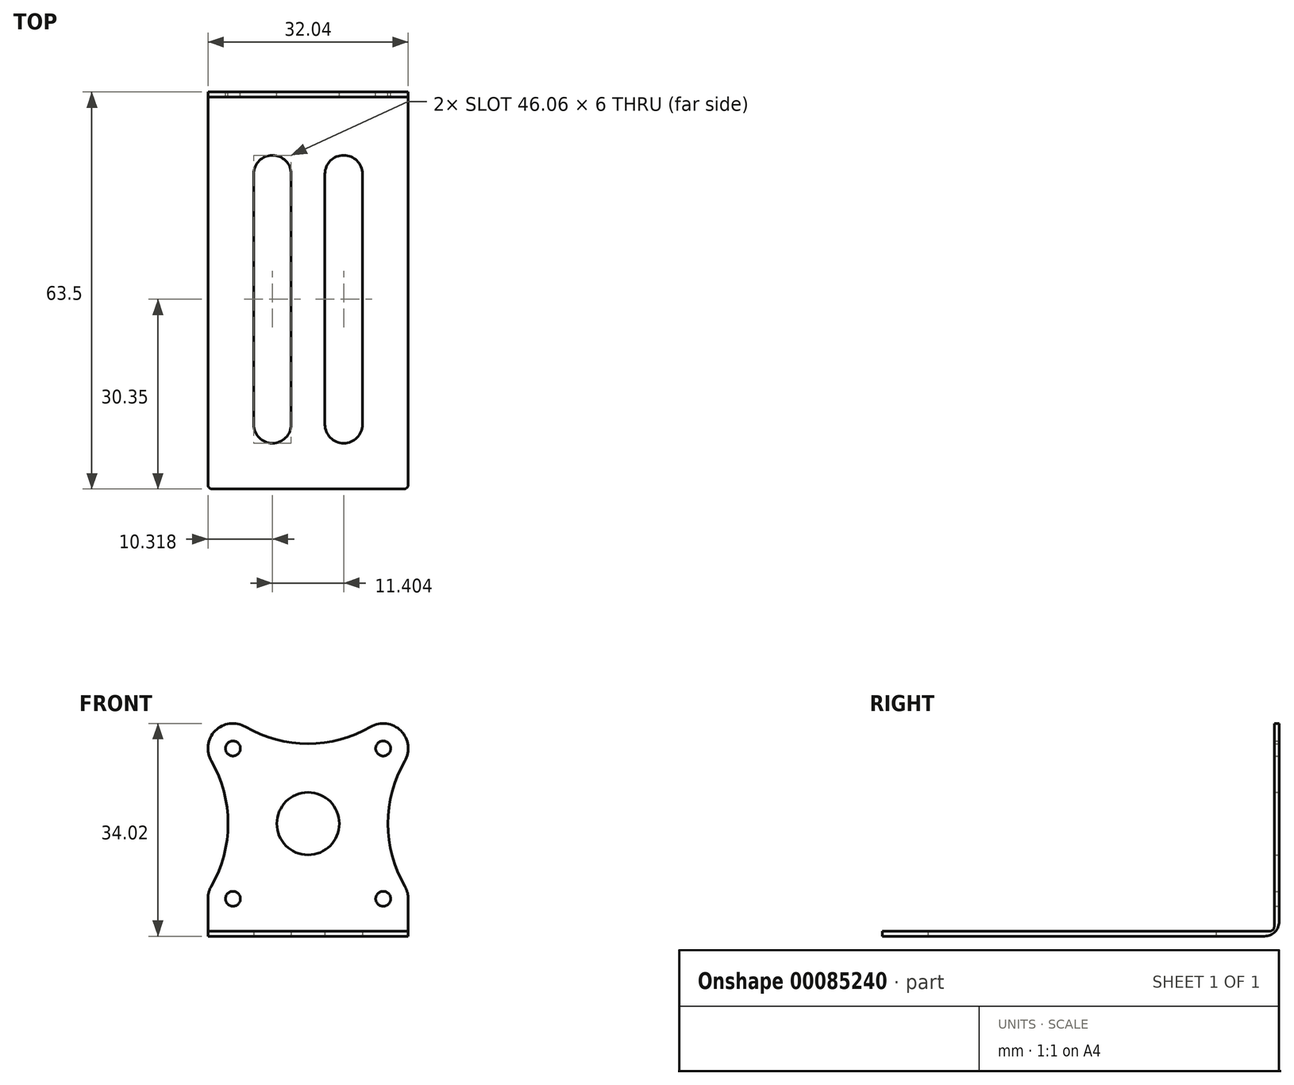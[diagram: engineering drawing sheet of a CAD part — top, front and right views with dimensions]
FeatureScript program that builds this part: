
annotation { "Feature Type Name" : "Feature", "Feature Type Description" : "" }
export const myFeature = defineFeature(function(context is Context, id is Id, definition is map)
    precondition{}
    {
        {
            assignVariable(context, id + "F0", {"name" : "thick", "anyValue" : .79});
        }
        {
            assignVariable(context, id + "F1", {"name" : "a", "anyValue" : .3125 + .375});
        }
        {
            var Q0;
            Q0=qCreatedBy(makeId("Front.planeOp"),FACE);
            var sketch = newSketch(context, id + "F2", { "sketchPlane" : qUnion([Q0])});
            skLineSegment(sketch, "E0.bottom", {"start": v(-12.02, 30.02) * mm, "end": v(12.02, 30.02) * mm, "construction": true});
            skLineSegment(sketch, "E0.top", {"start": v(-12.02, 5.98) * mm, "end": v(12.02, 5.98) * mm, "construction": true});
            skLineSegment(sketch, "E0.left", {"start": v(-12.02, 30.02) * mm, "end": v(-12.02, 5.98) * mm, "construction": true});
            skLineSegment(sketch, "E0.right", {"start": v(12.02, 30.02) * mm, "end": v(12.02, 5.98) * mm, "construction": true});
            skLineSegment(sketch, "E1", {"start": v(-12.02, 5.98) * mm, "end": v(12.02, 30.02) * mm, "construction": true});
            skPoint(sketch, "E2", {"position": v(0, 18) * mm});
            skCircle(sketch, "E3", {"center": v(-12.02, 30.02) * mm, "radius": 1.2 * mm});
            skCircle(sketch, "E4", {"center": v(12.02, 30.02) * mm, "radius": 1.2 * mm});
            skCircle(sketch, "E5", {"center": v(12.02, 5.98) * mm, "radius": 1.2 * mm});
            skCircle(sketch, "E6", {"center": v(-12.02, 5.98) * mm, "radius": 1.2 * mm});
            skCircle(sketch, "E7", {"center": v(0, 18) * mm, "radius": 14 * mm, "construction": true});
            skArc(sketch, "E8", {"start": v(-10.02, 33.48) * mm, "mid": v(0, 30.8) * mm, "end": v(10.02, 33.48) * mm});
            skArc(sketch, "E9", {"start": v(-15.48, 7.98) * mm, "mid": v(-12.8, 18) * mm, "end": v(-15.48, 28.02) * mm});
            skLineSegment(sketch, "E10", {"start": v(15.48, 28.02) * mm, "end": v(15.48, 28.02) * mm});
            skArc(sketch, "E11", {"start": v(-10.02, 33.48) * mm, "mid": v(-14.85, 32.85) * mm, "end": v(-15.48, 28.02) * mm});
            skArc(sketch, "E12", {"start": v(-15.48, 28.02) * mm, "mid": v(-9.2, 27.2) * mm, "end": v(-10.02, 33.48) * mm, "construction": true});
            skLineSegment(sketch, "E13", {"start": v(10.02, 33.48) * mm, "end": v(10.02, 33.48) * mm});
            skArc(sketch, "E14", {"start": v(15.48, 28.02) * mm, "mid": v(12.8, 18) * mm, "end": v(15.48, 7.98) * mm});
            skArc(sketch, "E15", {"start": v(-15.48, 7.98) * mm, "mid": v(-15.88, 7.02) * mm, "end": v(-16.02, 5.98) * mm});
            skArc(sketch, "E16", {"start": v(-16.02, 5.98) * mm, "mid": v(-8.16, 4.94) * mm, "end": v(-15.48, 7.98) * mm, "construction": true});
            skArc(sketch, "E17", {"start": v(15.48, 7.98) * mm, "mid": v(8.16, 4.94) * mm, "end": v(16.02, 5.98) * mm, "construction": true});
            skArc(sketch, "E18", {"start": v(16.02, 5.98) * mm, "mid": v(15.88, 7.02) * mm, "end": v(15.48, 7.98) * mm});
            skArc(sketch, "E19", {"start": v(10.02, 33.48) * mm, "mid": v(9.2, 27.2) * mm, "end": v(15.48, 28.02) * mm, "construction": true});
            skArc(sketch, "E20", {"start": v(15.48, 28.02) * mm, "mid": v(14.85, 32.85) * mm, "end": v(10.02, 33.48) * mm});
            skLineSegment(sketch, "E21", {"start": v(-16.02, 5.98) * mm, "end": v(-16.02, 0) * mm});
            skLineSegment(sketch, "E22", {"start": v(-16.02, 0) * mm, "end": v(16.02, 0) * mm});
            skLineSegment(sketch, "E23", {"start": v(16.02, 0) * mm, "end": v(16.02, 5.98) * mm});
            skCircle(sketch, "E24", {"center": v(0, 18) * mm, "radius": 5 * mm});
            skCircle(sketch, "E25", {"center": v(0, 18) * mm, "radius": 9.5 * mm, "construction": true});
            skCircle(sketch, "E26", {"center": v(0, 18) * mm, "radius": 8 * mm, "construction": true});
            skLineSegment(sketch, "E27", {"start": v(12.02, 5.98) * mm, "end": v(-12.02, 30.02) * mm, "construction": true});
            skSolve(sketch);
        }
        {
            var Q0;
            Q0 = qSketchRegion(id + "F2", true);
            extrude(context, id + "F3", {"entities" : qUnion([Q0]), "depth" : (getVariable(context, 'thick')) * mm});
        }
        {
            var Q0;
            Q0=qCreatedBy(makeId("Top.planeOp"),FACE);
            var sketch = newSketch(context, id + "F4", { "sketchPlane" : qUnion([Q0])});
            skLineSegment(sketch, "E28.bottom", {"start": v(-16.02, 0) * mm, "end": v(16.02, 0) * mm});
            skLineSegment(sketch, "E28.top", {"start": v(-16.02, -63.5) * mm, "end": v(16.02, -63.5) * mm});
            skLineSegment(sketch, "E28.left", {"start": v(-16.02, 0) * mm, "end": v(-16.02, -63.5) * mm});
            skLineSegment(sketch, "E28.right", {"start": v(16.02, 0) * mm, "end": v(16.02, -63.5) * mm});
            skSolve(sketch);
        }
        {
            var Q0;
            Q0 = qSketchRegion(id + "F4", true);
            extrude(context, id + "F5", {"entities" : qUnion([Q0]), "operationType" : NewBodyOperationType.ADD, "depth" : (getVariable(context, 'thick')) * mm});
        }
        {
            var Q0;
            Q0=makeQuery(id+"F5.boolean.opBoolean","INTERSECT",EDGE,{"derivedFrom":[makeQuery(id+"F3.opExtrude","CAP_FACE",FACE,{"disambiguationData":[OSD([sQuery(id+"F2.wireOp",EDGE,"E3"),sQuery(id+"F2.wireOp",EDGE,"E4"),sQuery(id+"F2.wireOp",EDGE,"E5"),sQuery(id+"F2.wireOp",EDGE,"E6"),sQuery(id+"F2.wireOp",EDGE,"E8"),sQuery(id+"F2.wireOp",EDGE,"E9"),sQuery(id+"F2.wireOp",EDGE,"E11"),sQuery(id+"F2.wireOp",EDGE,"E14"),sQuery(id+"F2.wireOp",EDGE,"E15"),sQuery(id+"F2.wireOp",EDGE,"E18"),sQuery(id+"F2.wireOp",EDGE,"E20"),sQuery(id+"F2.wireOp",EDGE,"E21"),sQuery(id+"F2.wireOp",EDGE,"E22"),sQuery(id+"F2.wireOp",EDGE,"E23")])],"isStart":false}),makeQuery(id+"F5.opExtrude","CAP_FACE",FACE,{"disambiguationData":[OSD([sQuery(id+"F4.wireOp",EDGE,"E28.bottom"),sQuery(id+"F4.wireOp",EDGE,"E28.top"),sQuery(id+"F4.wireOp",EDGE,"E28.left"),sQuery(id+"F4.wireOp",EDGE,"E28.right")])],"isStart":false})]});
            fillet(context, id + "F6", {"entities" : qUnion([Q0]), "radius" : 0.8 * mm, "tangentPropagation" : true, "allowEdgeOverflow" : false});
        }
        {
            var Q0;
            Q0=makeQuery(id+"F3.opExtrude","CAP_EDGE",EDGE,{"disambiguationData":[OSD([sQuery(id+"F2.wireOp",EDGE,"E22")])],"isStart":true});
            fillet(context, id + "F7", {"entities" : qUnion([Q0]), "radius" : 2.38 * mm, "tangentPropagation" : true, "allowEdgeOverflow" : false});
        }
        {
            var Q0;
            Q0=makeQuery(id+"F5.opExtrude","SWEPT_EDGE",EDGE,{"disambiguationData":[OSD([sQuery(id+"F4.wireOp",EDGE,"E28.top"),sQuery(id+"F4.wireOp",EDGE,"E28.right")])]});
            var Q1;
            Q1=makeQuery(id+"F5.opExtrude","SWEPT_EDGE",EDGE,{"disambiguationData":[OSD([sQuery(id+"F4.wireOp",EDGE,"E28.top"),sQuery(id+"F4.wireOp",EDGE,"E28.left")])]});
            fillet(context, id + "F8", {"entities" : qUnion([Q0, Q1]), "radius" : (getVariable(context, 'a')) * mm, "tangentPropagation" : true, "allowEdgeOverflow" : false});
        }
        {
            var Q0;
            Q0=makeQuery(id+"F5.boolean.opBoolean","MERGE",FACE,{"derivedFrom":[makeQuery(id+"F3.opExtrude","SWEPT_FACE",FACE,{"disambiguationData":[OSD([sQuery(id+"F2.wireOp",EDGE,"E22")])]}),makeQuery(id+"F5.opExtrude","CAP_FACE",FACE,{"disambiguationData":[OSD([sQuery(id+"F4.wireOp",EDGE,"E28.bottom"),sQuery(id+"F4.wireOp",EDGE,"E28.top"),sQuery(id+"F4.wireOp",EDGE,"E28.left"),sQuery(id+"F4.wireOp",EDGE,"E28.right")])],"isStart":true})]});
            var sketch = newSketch(context, id + "F9", { "sketchPlane" : qUnion([Q0])});
            skArc(sketch, "E29.0", {"start": v(8.7, 53.18) * mm, "mid": v(5.7, 56.18) * mm, "end": v(2.7, 53.18) * mm});
            skLineSegment(sketch, "E29.2", {"start": v(-8.7, 53.18) * mm, "end": v(-8.7, 13.12) * mm});
            skLineSegment(sketch, "E29.3", {"start": v(8.7, 53.18) * mm, "end": v(8.7, 13.12) * mm});
            skArc(sketch, "E29.4", {"start": v(-2.7, 53.18) * mm, "mid": v(-5.7, 56.18) * mm, "end": v(-8.7, 53.18) * mm});
            skArc(sketch, "E30.filletArc", {"start": v(-8.7, 13.12) * mm, "mid": v(-5.7, 10.12) * mm, "end": v(-2.7, 13.12) * mm});
            skArc(sketch, "E31.filletArc", {"start": v(2.7, 13.12) * mm, "mid": v(5.7, 10.12) * mm, "end": v(8.7, 13.12) * mm});
            skLineSegment(sketch, "E32", {"start": v(-2.7, 13.12) * mm, "end": v(-2.7, 53.18) * mm});
            skLineSegment(sketch, "E33", {"start": v(2.7, 13.12) * mm, "end": v(2.7, 53.18) * mm});
            skLineSegment(sketch, "E34", {"start": v(-5.7, 56.18) * mm, "end": v(-5.7, 63.5) * mm, "construction": true});
            skLineSegment(sketch, "E35", {"start": v(-5.7, 10.12) * mm, "end": v(-5.7, 2.8) * mm, "construction": true});
            skSolve(sketch);
        }
        {
            var Q0;
            Q0 = qSketchRegion(id + "F9", true);
            extrude(context, id + "F10", {"entities" : qUnion([Q0]), "operationType" : NewBodyOperationType.REMOVE, "endBound" : BoundingType.UP_TO_NEXT, "oppositeDirection" : true, "depth" : 25.4 * mm});
        }
    });
